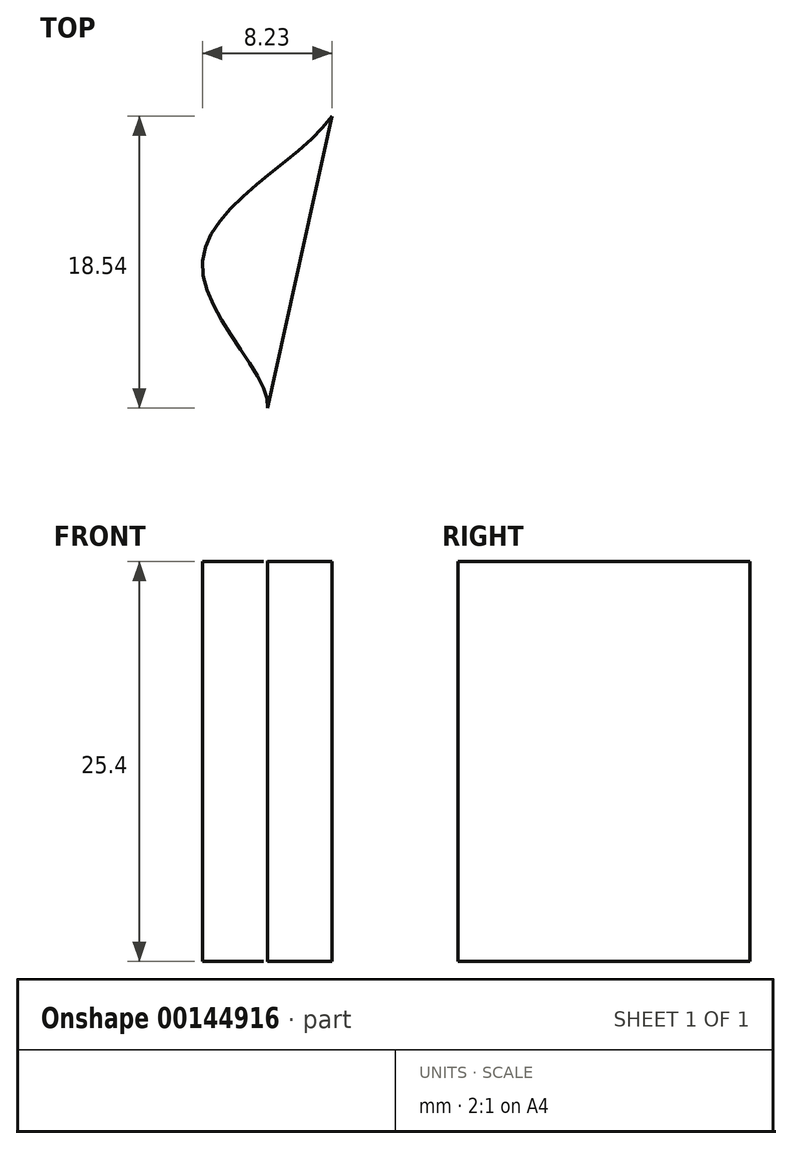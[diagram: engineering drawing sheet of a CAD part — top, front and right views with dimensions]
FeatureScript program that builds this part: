
annotation { "Feature Type Name" : "Feature", "Feature Type Description" : "" }
export const myFeature = defineFeature(function(context is Context, id is Id, definition is map)
    precondition{}
    {
        {
            var Q0;
            Q0=qCreatedBy(makeId("Top.planeOp"),FACE);
            var sketch = newSketch(context, id + "F0", { "sketchPlane" : qUnion([Q0])});
            skFitSpline(sketch, "E0", {"points": [v(-77.62, 35.3) * mm, v(-84.05, 31.98) * mm, v(-82.53, 22.1) * mm, v(-64.14, 19) * mm, v(-61.96, 15.5) * mm, v(-67.03, 12.78) * mm, v(-71.76, 9.37) * mm, v(-77.5, 3.76) * mm, v(-77.23, 0) * mm, v(-70.5, -3.46) * mm, v(-53.6, 3.21) * mm, v(-47.57, -2.45) * mm, v(-31.5, -13.88) * mm, v(-29.33, -20.34) * mm, v(-21.9, -25.65) * mm, v(-30.93, -30.8) * mm, v(-33.33, -31.98) * mm, v(-35.17, -34.1) * mm, v(-35.44, -37.78) * mm, v(-32.53, -39.44) * mm, v(-29.95, -37.56) * mm, v(-23.3, -33.07) * mm, v(-15.68, -31.11) * mm, v(-12.75, -28.2) * mm, v(-9.29, -29.92) * mm, v(-11.7, -34.9) * mm, v(-14.36, -38.57) * mm, v(-15.94, -42.26) * mm, v(-13.3, -44.63) * mm, v(-9.1, -41.47) * mm, v(-7.78, -38.04) * mm, v(-5.76, -35.84) * mm, v(-3.18, -35.85) * mm, v(0, -38.38) * mm, v(4.32, -48.86) * mm, v(8.23, -59.1) * mm, v(8.23, -66.37) * mm, v(0, -75.72) * mm, v(4.12, -84.97) * mm, v(-4.59, -88.47) * mm, v(-6.22, -94.24) * mm, v(10.4, -94.24) * mm, v(14.77, -84.19) * mm, v(17, -68.08) * mm, v(18.78, -59.06) * mm, v(18.06, -55.22) * mm, v(17.86, -43.14) * mm, v(29.9, -43.91) * mm, v(34.33, -47.75) * mm, v(47.54, -58.33) * mm, v(58.05, -68.89) * mm, v(62.22, -79.15) * mm, v(59.08, -86.96) * mm, v(47.57, -89.49) * mm, v(44.3, -94.24) * mm, v(50.15, -94.24) * mm, v(59.15, -94.24) * mm, v(64.94, -95.25) * mm, v(68.94, -89.99) * mm, v(71.62, -86.07) * mm, v(73.71, -80.75) * mm, v(74.17, -72.29) * mm, v(72.3, -66.18) * mm, v(65.19, -54.4) * mm, v(61.2, -45.97) * mm, v(61.09, -38.52) * mm, v(56.02, -35.94) * mm, v(62.59, -31.13) * mm, v(92.57, -26.43) * mm, v(116.3, -32.21) * mm, v(129.5, -44.33) * mm, v(133.2, -58.31) * mm, v(130.26, -68.36) * mm, v(121.86, -82.85) * mm, v(109.96, -88.9) * mm, v(92.37, -93.35) * mm, v(86.07, -94.43) * mm, v(120.24, -95.5) * mm, v(138.18, -80.73) * mm, v(148.99, -53.6) * mm, v(145.3, -34.86) * mm, v(132.63, -18.78) * mm, v(108.39, -8.8) * mm, v(82.57, -2.75) * mm, v(56.51, 5.67) * mm, v(42.8, 11.51) * mm, v(28.28, 11.47) * mm, v(0, 14.1) * mm, v(-10.4, 15.51) * mm, v(-15.67, 12.16) * mm, v(-22.08, 14.59) * mm, v(-25.68, 23.62) * mm, v(-33.3, 34.41) * mm, v(-43.05, 41.57) * mm, v(-54.66, 40.71) * mm, v(-65.68, 40.12) * mm, v(-69.73, 42.1) * mm, v(-82.47, 43.19) * mm, v(-77.62, 35.3) * mm]});
            skLineSegment(sketch, "E1", {"start": v(59.15, -94.24) * mm, "end": v(62.29, -101.52) * mm});
            skLineSegment(sketch, "E2", {"start": v(-43.76, -94.24) * mm, "end": v(147.63, -94.24) * mm});
            skLineSegment(sketch, "E3", {"start": v(8.23, -66.37) * mm, "end": v(4.12, -84.97) * mm});
            skSolve(sketch);
        }
        {
            var Q0;
            {var subQ0=sQuery(id+"F0.wireOp",EDGE,"E3");var subQ1=sQuery(id+"F0.wireOp",EDGE,"E0");var subQ8=makeQuery(id+"F0.imprint","INTERSECT",VERTEX,{"disambiguationData":[OD(0.0)],"derivedFrom":[subQ1,subQ0]});Q0=makeQuery(id+"F0.imprint","IMPRINT",FACE,{"disambiguationData":[TD([[makeQuery(id+"F0.imprint","IMPRINT",EDGE,{"disambiguationData":[TD([[subQ8,-1.0]])],"derivedFrom":subQ1}),1.0]])]});}
            extrude(context, id + "F1", {"entities" : qUnion([Q0]), "depth" : 25.4 * mm});
        }
    });
